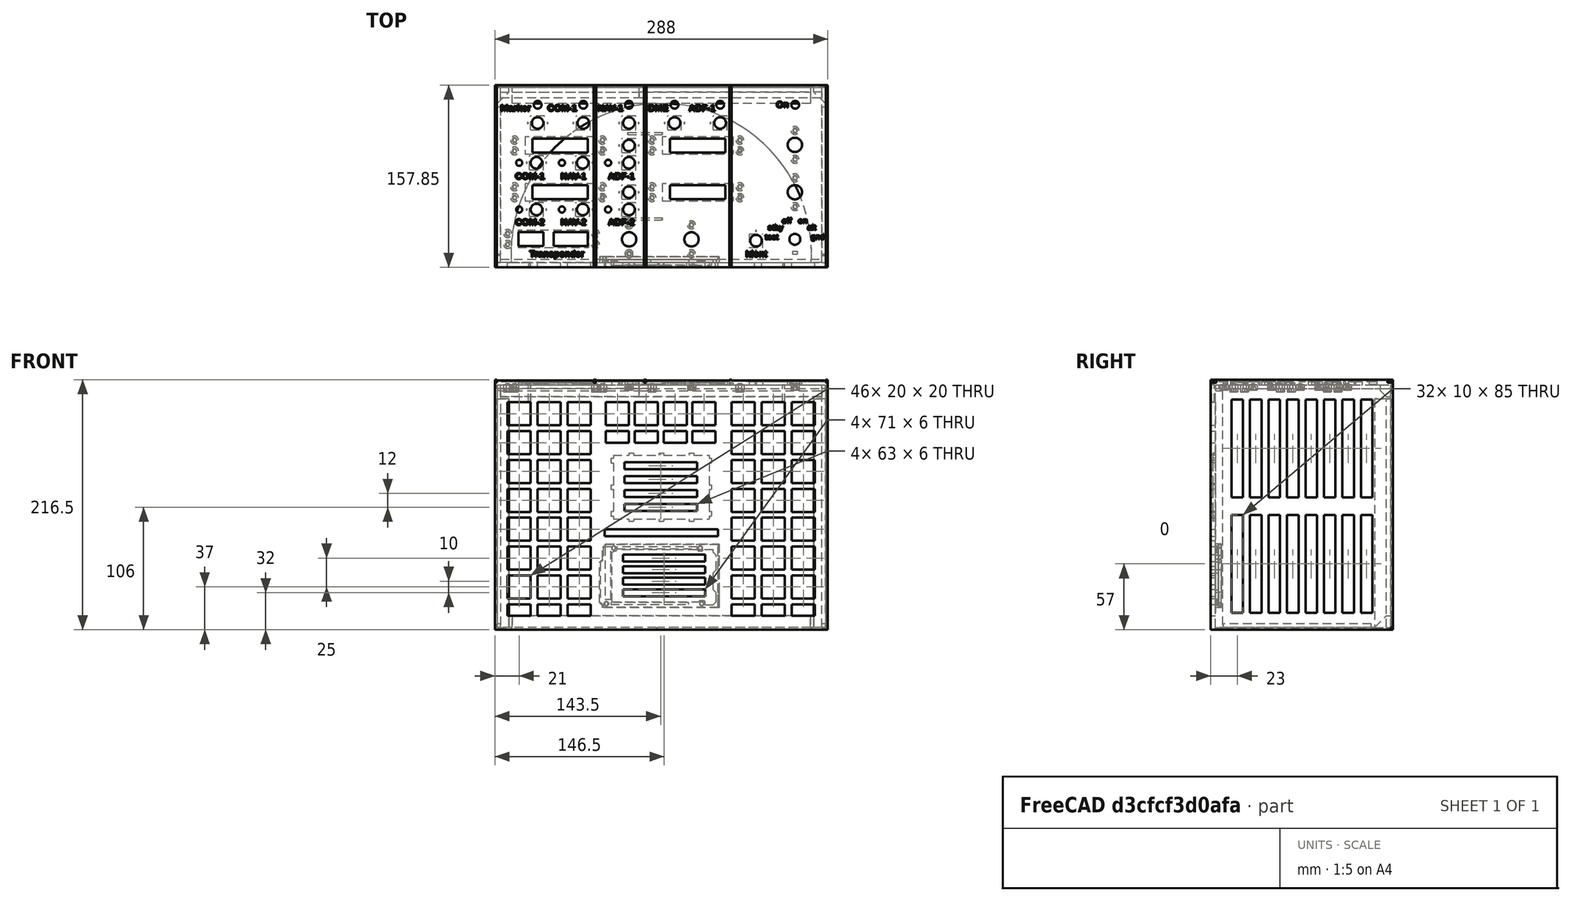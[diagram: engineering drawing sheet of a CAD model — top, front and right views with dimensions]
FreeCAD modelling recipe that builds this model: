
FCSTD DOCUMENT  (FreeCAD 0.17R13522 (Git))
Label: panel_base_y_latererales
License: CreativeCommons Attribution-ShareAlike
LicenseURL: http://creativecommons.org/licenses/by-sa/4.0/
objects: Part::Feature×3, Part::Fuse×1
note: 4 computed .brp shape members not serialized (recipe doc carries the construction recipe); baked Part::Feature solids carry a one-line shape summary decoded from their .brp

FEATURE [Part::Feature] Fusion001001009001003001  label="panel_base_y_laterales"
  shape: bbox 288 x 157.9 x 216.5 mm, 3301 faces (baked)
FEATURE [Part::Feature] Fusion002002005001003001  label="pared_fondo"
  Placement = pos=(288,151.85,-319) rot=(0,0,1;3.14159rad)
  shape: bbox 288 x 151.9 x 12 mm, 25 faces (baked)
FEATURE [Part::Fuse] Fusion  label="caja_sin_techo"
  Base = -> Fusion001001009001003001
  Refine = true
  Tool = -> Fusion002002005001003001
FEATURE [Part::Feature] Fusion001007001  label="tapa_entera002"
  Placement = pos=(2,153.85,-319) rot=(1,0,0;1.5708rad)
  shape: bbox 288 x 2 x 212 mm, 10 faces (baked)
